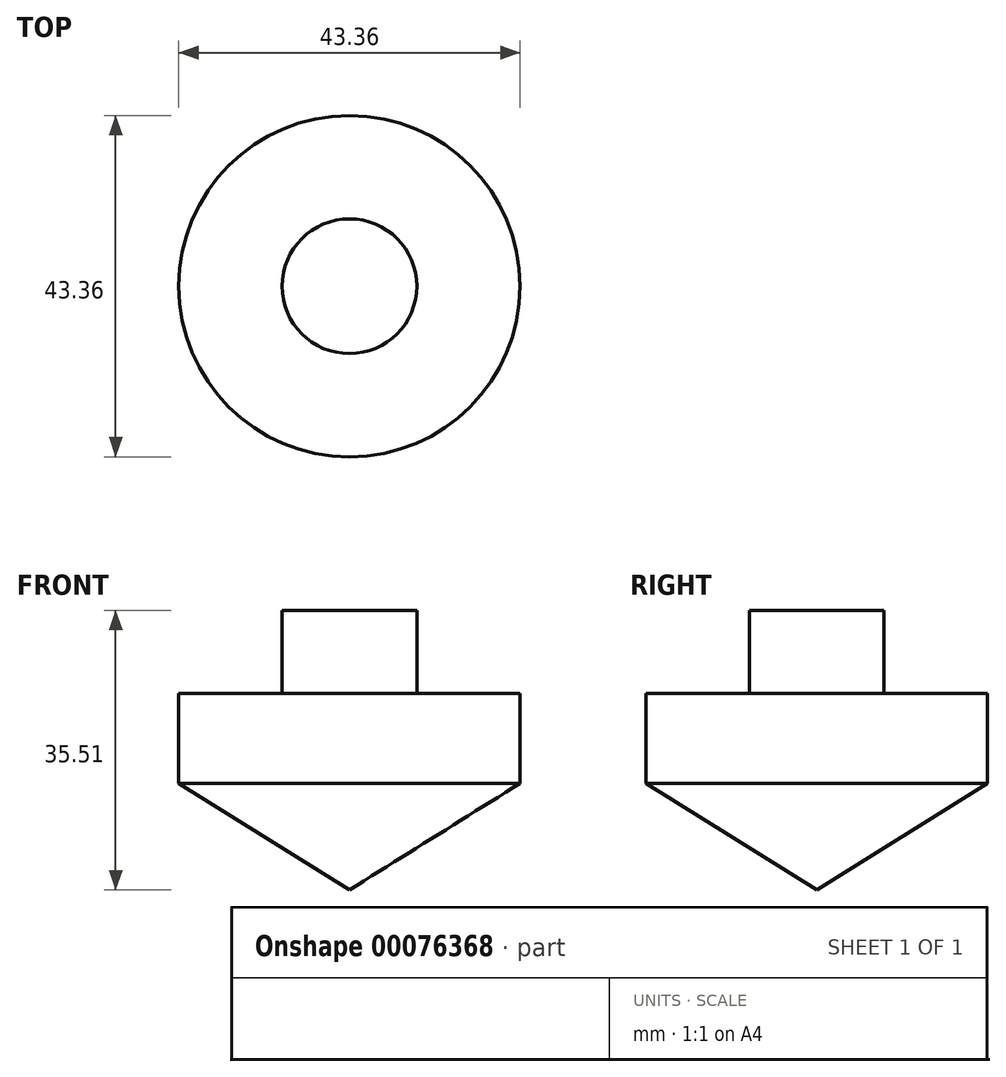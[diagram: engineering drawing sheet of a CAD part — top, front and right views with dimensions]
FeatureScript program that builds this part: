
annotation { "Feature Type Name" : "Feature", "Feature Type Description" : "" }
export const myFeature = defineFeature(function(context is Context, id is Id, definition is map)
    precondition{}
    {
        {
            var Q0;
            Q0=qCreatedBy(makeId("Front.planeOp"),FACE);
            var sketch = newSketch(context, id + "F0", { "sketchPlane" : qUnion([Q0])});
            skLineSegment(sketch, "E0", {"start": v(0, 0) * mm, "end": v(21.68, 13.55) * mm});
            skLineSegment(sketch, "E1", {"start": v(21.68, 13.55) * mm, "end": v(21.68, 24.96) * mm});
            skLineSegment(sketch, "E2", {"start": v(21.68, 24.96) * mm, "end": v(8.56, 24.96) * mm});
            skLineSegment(sketch, "E3", {"start": v(8.56, 24.96) * mm, "end": v(8.56, 35.51) * mm});
            skLineSegment(sketch, "E4", {"start": v(8.56, 35.51) * mm, "end": v(0, 35.51) * mm});
            skLineSegment(sketch, "E5", {"start": v(0, 35.51) * mm, "end": v(0, 0) * mm});
            skSolve(sketch);
        }
        {
            var Q0;
            Q0 = qSketchRegion(id + "F0", true);
            var Q1;
            Q1=sQuery(id+"F0.wireOp",EDGE,"E5");
            revolve(context, id + "F1", {"entities" : qUnion([Q0]), "axis" : qUnion([Q1]), "revolveType" : RevolveType.FULL});
        }
    });
